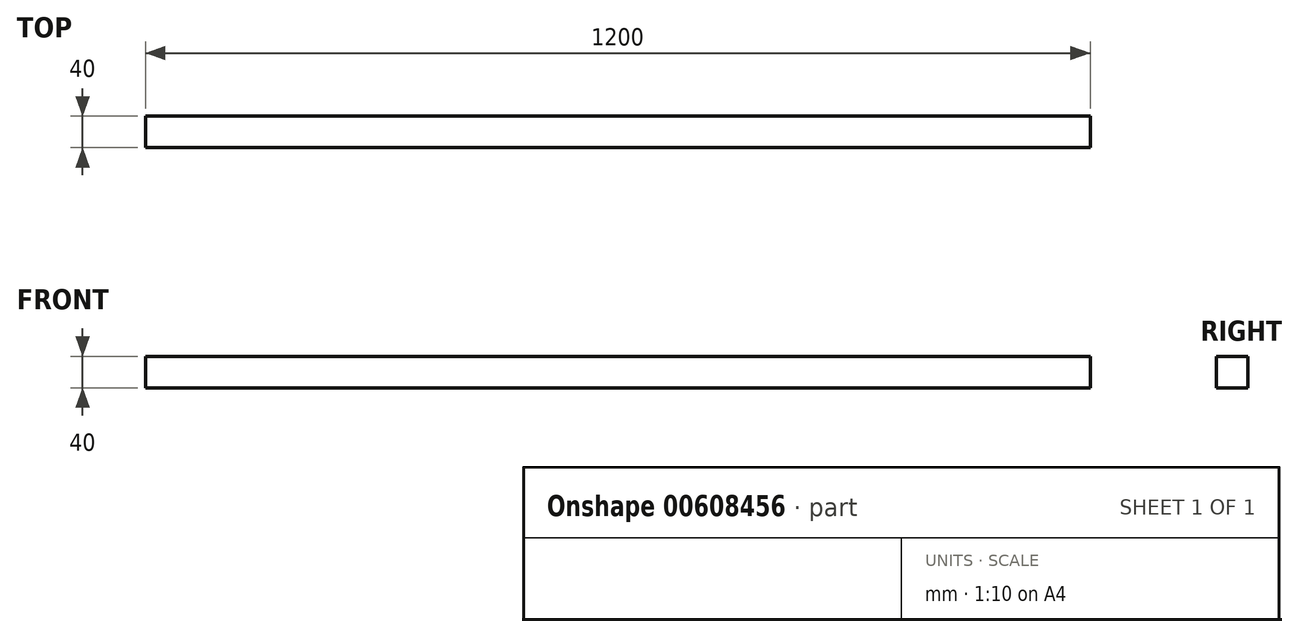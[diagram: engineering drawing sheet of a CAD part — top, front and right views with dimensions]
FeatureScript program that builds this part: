
annotation { "Feature Type Name" : "Feature", "Feature Type Description" : "" }
export const myFeature = defineFeature(function(context is Context, id is Id, definition is map)
    precondition{}
    {
        {
            var Q0;
            Q0=qCreatedBy(makeId("Front.planeOp"),FACE);
            var sketch = newSketch(context, id + "F0", { "sketchPlane" : qUnion([Q0])});
            skLineSegment(sketch, "E0.bottom", {"start": v(-564.25, 24.67) * mm, "end": v(635.75, 24.67) * mm});
            skLineSegment(sketch, "E0.top", {"start": v(-564.25, -15.33) * mm, "end": v(635.75, -15.33) * mm});
            skLineSegment(sketch, "E0.left", {"start": v(-564.25, 24.67) * mm, "end": v(-564.25, -15.33) * mm});
            skLineSegment(sketch, "E0.right", {"start": v(635.75, 24.67) * mm, "end": v(635.75, -15.33) * mm});
            skSolve(sketch);
        }
        {
            var Q0;
            Q0=makeQuery(id+"F0.imprint","IMPRINT",FACE,{"disambiguationData":[TD([[makeQuery(id+"F0.imprint","IMPRINT",EDGE,{"derivedFrom":sQuery(id+"F0.wireOp",EDGE,"E0.bottom")}),-1.0]])]});
            extrude(context, id + "F1", {"entities" : qUnion([Q0]), "depth" : 40 * mm, "offsetDistance" : 25 * mm});
        }
    });
